# Revit family: NBS_Allermuir_DmstcChrs_Jinx-en-us_JNX01
name_source: partatom
category: Furniture
revit_build: Autodesk Revit 2016 (Build: 20151007_0715(x64)
units: mm (PartAtom-declared; Revit-internal decimal feet)

## family parameters
Always vertical = Yes
Cut with Voids When Loaded = No
Room Calculation Point = No
Shared = No
Work Plane-Based = No

## types (1)
- JNX01
    AssetType = Moveable
    BIMObjectName = NBS_Allermuir_DomesticChairs_Jinx_JNX01-US
    Category = Pr_40_50_12_22:Dining chairs
    CodePerformance = ANSI/BIFMA X5.4: 2012
    Description = Lounge chair
    DurationUnit = year
    EnvironmentalProductDeclaration = http://www.thesenatorgroup.com
    ExpectedLife = 5
    Features = Wood carcass construction, dual desinsity back foam, sprung seat foam, fully upholstered, platic glides, swivel base, solid ash side shelf with a clear finish, ash side shelf can be stainged or color washed, plastic glides with felt, two tone upholstery
    FramesMaterial = Wood
    HasShelf = Yes
    HighestSeatingHeight = 0 "
    IfcExportAs = IfcFurnitureType
    IfcExportType = SOFA
    IsBuiltIn = No
    LowestSeatingHeight = 0 "
    ManufacturerName = Allermuir
    ManufacturerURL = http://www.thesenatorgroup.com
    ModelNumber = JNX01
    ModelReference = Jinx
    NBSCertification = www.nationalbimlibrary.com/cert/fmfp3dwp
    NBSDescription = Domestic chairs
    NBSReference = 45-35-20/365
    Name = DomesticChairs_Jinx_JNX01-US_Allermuir
    NominalDepth = 40 "
    NominalHeight = 26 "
    NominalLength = 38 "
    NominalWidth = 40 "
    OmniClassCode = 22-12 52 23
    OmniClassTitle = Office Seating
    OmniClassVersion = Table 22 2012-05-16
    ProductInformation = http://www.thesenatorgroup.com
    SeatingHeight = 16 "
    SeatingSeatMaterial = NBS_Concept
    SeatsAndBacksMaterial = Upholstered
    ShelfMaterial = NBS_Concept
    Size = 38 X 39.5 X 26.35"
    Status = UNSET
    Uniclass2015Code = Pr_40_50_12_22
    Uniclass2015Title = Dining chairs
    Uniclass2015Version = Products v1.9
    Version = 1
    WarrantyDescription = Allermuir warrant that its manufactured products are free from manufacturing defects in materials or workmanship for a period of ten years
    WarrantyDurationParts = 10
    WarrantyDurationUnit = year

## geometry (parser evidence)
native form markers: Sweep x2
no freeform markers — native parametric forms only
